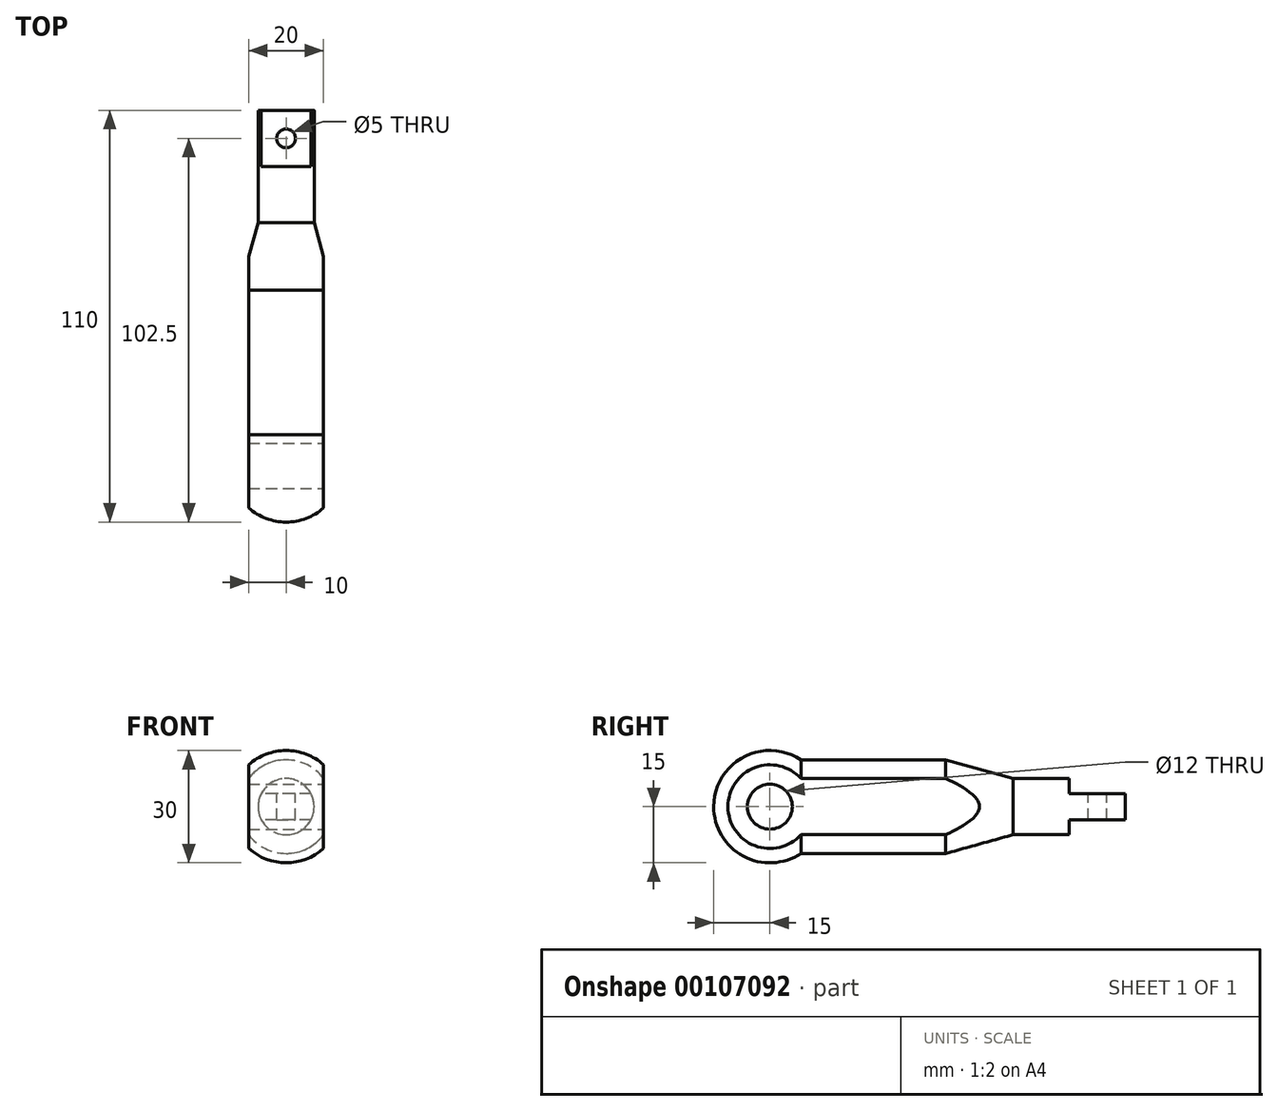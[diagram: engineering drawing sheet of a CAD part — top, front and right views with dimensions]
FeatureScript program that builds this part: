
annotation { "Feature Type Name" : "Feature", "Feature Type Description" : "" }
export const myFeature = defineFeature(function(context is Context, id is Id, definition is map)
    precondition{}
    {
        {
            var Q0;
            Q0=qCreatedBy(makeId("Right.planeOp"),FACE);
            var sketch = newSketch(context, id + "F0", { "sketchPlane" : qUnion([Q0])});
            skLineSegment(sketch, "E0", {"start": v(-23.72, 0) * mm, "end": v(99.33, 0) * mm, "construction": true});
            skLineSegment(sketch, "E1", {"start": v(8.3, 12.5) * mm, "end": v(47, 12.5) * mm});
            skLineSegment(sketch, "E2", {"start": v(47, 12.5) * mm, "end": v(65, 7.5) * mm});
            skLineSegment(sketch, "E3", {"start": v(65, 7.5) * mm, "end": v(95, 7.5) * mm});
            skLineSegment(sketch, "E4", {"start": v(95, 7.5) * mm, "end": v(95, 0) * mm});
            skLineSegment(sketch, "E5", {"start": v(-15, 0) * mm, "end": v(95, 0) * mm});
            skArc(sketch, "E6", {"start": v(8.3, 12.5) * mm, "mid": v(-7.1, 13.22) * mm, "end": v(-15, 0) * mm});
            skSolve(sketch);
        }
        {
            var Q0;
            Q0=makeQuery(id+"F0.imprint","IMPRINT",FACE,{"disambiguationData":[TD([[makeQuery(id+"F0.imprint","IMPRINT",EDGE,{"derivedFrom":sQuery(id+"F0.wireOp",EDGE,"E1")}),-1.0]])]});
            var Q1;
            Q1=sQuery(id+"F0.wireOp",EDGE,"E0");
            revolve(context, id + "F1", {"entities" : qUnion([Q0]), "axis" : qUnion([Q1]), "revolveType" : RevolveType.FULL});
        }
        {
            var Q0;
            Q0=makeQuery(id+"F1.opRevolve","SWEPT_FACE",FACE,{"disambiguationData":[OSD([sQuery(id+"F0.wireOp",EDGE,"E4")])]});
            var sketch = newSketch(context, id + "F2", { "sketchPlane" : qUnion([Q0])});
            skLineSegment(sketch, "E7", {"start": v(-6.63, 3.5) * mm, "end": v(6.63, 3.5) * mm});
            skLineSegment(sketch, "E8", {"start": v(-6.63, -3.5) * mm, "end": v(6.63, -3.5) * mm});
            skSolve(sketch);
        }
        {
            var Q0;
            {var subQ0=sQuery(id+"F2.wireOp",EDGE,"E7");Q0=makeQuery(id+"F2.imprint","IMPRINT",FACE,{"disambiguationData":[TD([[makeQuery(id+"F2.imprint","IMPRINT",EDGE,{"derivedFrom":subQ0}),1.0]])]});}
            var Q1;
            {var subQ0=sQuery(id+"F2.wireOp",EDGE,"E8");Q1=makeQuery(id+"F2.imprint","IMPRINT",FACE,{"disambiguationData":[TD([[makeQuery(id+"F2.imprint","IMPRINT",EDGE,{"derivedFrom":subQ0}),-1.0]])]});}
            extrude(context, id + "F3", {"entities" : qUnion([Q0, Q1]), "operationType" : NewBodyOperationType.REMOVE, "oppositeDirection" : true, "depth" : 15 * mm});
        }
        {
            var Q0;
            Q0=makeQuery(id+"F3.boolean.opBoolean","COPY",FACE,{"derivedFrom":makeQuery(id+"F3.opExtrude","SWEPT_FACE",FACE,{"disambiguationData":[OSD([sQuery(id+"F2.wireOp",EDGE,"E7")])]})});
            var sketch = newSketch(context, id + "F4", { "sketchPlane" : qUnion([Q0])});
            skCircle(sketch, "E9", {"center": v(0, 87.5) * mm, "radius": 2.5 * mm});
            skSolve(sketch);
        }
        {
            var Q0;
            Q0=makeQuery(id+"F4.imprint","IMPRINT",FACE,{"disambiguationData":[TD([[makeQuery(id+"F4.imprint","IMPRINT",EDGE,{"derivedFrom":sQuery(id+"F4.wireOp",EDGE,"E9")}),1.0]])]});
            extrude(context, id + "F5", {"entities" : qUnion([Q0]), "operationType" : NewBodyOperationType.REMOVE, "endBound" : BoundingType.THROUGH_ALL, "oppositeDirection" : true, "depth" : 25 * mm});
        }
        {
            var Q0;
            Q0=qCreatedBy(makeId("Front.planeOp"),FACE);
            var sketch = newSketch(context, id + "F6", { "sketchPlane" : qUnion([Q0])});
            skLineSegment(sketch, "E10.bottom", {"start": v(-26.32, 26.04) * mm, "end": v(-10, 26.04) * mm});
            skLineSegment(sketch, "E10.top", {"start": v(-26.32, -33.73) * mm, "end": v(-10, -33.73) * mm});
            skLineSegment(sketch, "E10.left", {"start": v(-26.32, 26.04) * mm, "end": v(-26.32, -33.73) * mm});
            skLineSegment(sketch, "E10.right", {"start": v(-10, 26.04) * mm, "end": v(-10, -33.73) * mm});
            skLineSegment(sketch, "E11.bottom", {"start": v(10, 26.5) * mm, "end": v(30, 26.5) * mm});
            skLineSegment(sketch, "E11.top", {"start": v(10, -33.73) * mm, "end": v(30, -33.73) * mm});
            skLineSegment(sketch, "E11.left", {"start": v(10, 26.5) * mm, "end": v(10, -33.73) * mm});
            skLineSegment(sketch, "E11.right", {"start": v(30, 26.5) * mm, "end": v(30, -33.73) * mm});
            skSolve(sketch);
        }
        {
            var Q0;
            Q0=makeQuery(id+"F6.imprint","IMPRINT",FACE,{"disambiguationData":[TD([[makeQuery(id+"F6.imprint","IMPRINT",EDGE,{"derivedFrom":sQuery(id+"F6.wireOp",EDGE,"E10.bottom")}),-1.0]])]});
            var Q1;
            Q1=makeQuery(id+"F6.imprint","IMPRINT",FACE,{"disambiguationData":[TD([[makeQuery(id+"F6.imprint","IMPRINT",EDGE,{"derivedFrom":sQuery(id+"F6.wireOp",EDGE,"E11.bottom")}),-1.0]])]});
            extrude(context, id + "F7", {"entities" : qUnion([Q0, Q1]), "operationType" : NewBodyOperationType.REMOVE, "endBound" : BoundingType.SYMMETRIC, "depth" : 500 * mm});
        }
        {
            var Q0;
            Q0=makeQuery(id+"F7.boolean.opBoolean","COPY",FACE,{"derivedFrom":makeQuery(id+"F7.opExtrude","SWEPT_FACE",FACE,{"disambiguationData":[OSD([sQuery(id+"F6.wireOp",EDGE,"E11.left")])]})});
            var sketch = newSketch(context, id + "F8", { "sketchPlane" : qUnion([Q0])});
            skCircle(sketch, "E12", {"center": v(0, 0) * mm, "radius": 6 * mm});
            skSolve(sketch);
        }
        {
            var Q0;
            Q0=makeQuery(id+"F8.imprint","IMPRINT",FACE,{"disambiguationData":[TD([[makeQuery(id+"F8.imprint","IMPRINT",EDGE,{"derivedFrom":sQuery(id+"F8.wireOp",EDGE,"E12")}),1.0]])]});
            extrude(context, id + "F9", {"entities" : qUnion([Q0]), "operationType" : NewBodyOperationType.REMOVE, "endBound" : BoundingType.THROUGH_ALL, "oppositeDirection" : true, "depth" : 25 * mm});
        }
    });
